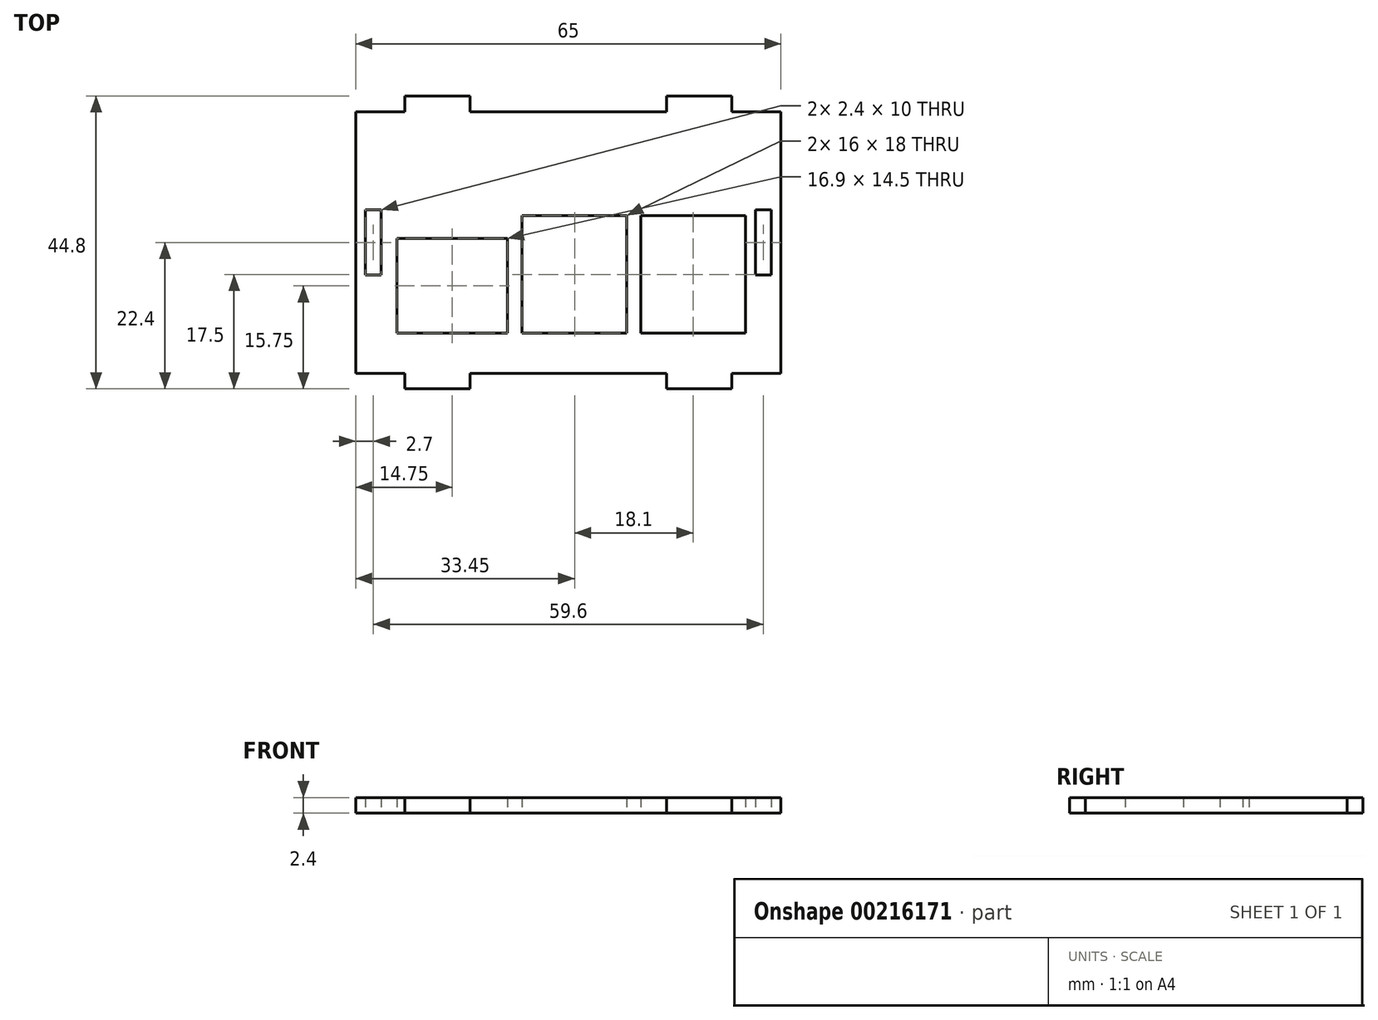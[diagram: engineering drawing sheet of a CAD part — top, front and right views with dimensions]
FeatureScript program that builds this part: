
annotation { "Feature Type Name" : "Feature", "Feature Type Description" : "" }
export const myFeature = defineFeature(function(context is Context, id is Id, definition is map)
    precondition{}
    {
        {
            var Q0;
            Q0=qCreatedBy(makeId("Top.planeOp"),FACE);
            var sketch = newSketch(context, id + "F0", { "sketchPlane" : qUnion([Q0])});
            skLineSegment(sketch, "E0.bottom", {"start": v(32.5, 20) * mm, "end": v(25, 20) * mm});
            skLineSegment(sketch, "E0.top", {"start": v(32.5, -20) * mm, "end": v(25, -20) * mm});
            skLineSegment(sketch, "E0.left", {"start": v(32.5, 20) * mm, "end": v(32.5, -20) * mm});
            skLineSegment(sketch, "E0.right", {"start": v(-32.5, 20) * mm, "end": v(-32.5, -20) * mm});
            skPoint(sketch, "E0.middle", {"position": v(0, 0) * mm});
            skLineSegment(sketch, "E1.bottom", {"start": v(-15, 22.4) * mm, "end": v(-25, 22.4) * mm});
            skLineSegment(sketch, "E1.left", {"start": v(-15, 22.4) * mm, "end": v(-15, 20) * mm});
            skLineSegment(sketch, "E1.right", {"start": v(-25, 22.4) * mm, "end": v(-25, 20) * mm});
            skPoint(sketch, "E1.middle", {"position": v(-20, 20) * mm});
            skLineSegment(sketch, "E2.bottom", {"start": v(25, 22.4) * mm, "end": v(15, 22.4) * mm});
            skLineSegment(sketch, "E2.left", {"start": v(25, 22.4) * mm, "end": v(25, 20) * mm});
            skLineSegment(sketch, "E2.right", {"start": v(15, 22.4) * mm, "end": v(15, 20) * mm});
            skPoint(sketch, "E2.middle", {"position": v(20, 20) * mm});
            skLineSegment(sketch, "E3.top", {"start": v(-15, -22.4) * mm, "end": v(-25, -22.4) * mm});
            skLineSegment(sketch, "E3.left", {"start": v(-15, -20) * mm, "end": v(-15, -22.4) * mm});
            skLineSegment(sketch, "E3.right", {"start": v(-25, -20) * mm, "end": v(-25, -22.4) * mm});
            skPoint(sketch, "E3.middle", {"position": v(-20, -20) * mm});
            skLineSegment(sketch, "E4.top", {"start": v(25, -22.4) * mm, "end": v(15, -22.4) * mm});
            skLineSegment(sketch, "E4.left", {"start": v(25, -20) * mm, "end": v(25, -22.4) * mm});
            skLineSegment(sketch, "E4.right", {"start": v(15, -20) * mm, "end": v(15, -22.4) * mm});
            skPoint(sketch, "E4.middle", {"position": v(20, -20) * mm});
            skPoint(sketch, "E5.middle", {"position": v(0, -20) * mm});
            skLineSegment(sketch, "E6.trimOffspring", {"start": v(-25, 20) * mm, "end": v(-32.5, 20) * mm});
            skLineSegment(sketch, "E7.trimOffspring", {"start": v(15, 20) * mm, "end": v(-15, 20) * mm});
            skLineSegment(sketch, "E8.trimOffspring", {"start": v(15, -20) * mm, "end": v(7.5, -20) * mm});
            skLineSegment(sketch, "E9.trimOffspring", {"start": v(7.5, -20) * mm, "end": v(-15, -20) * mm});
            skLineSegment(sketch, "E10.trimOffspring", {"start": v(-25, -20) * mm, "end": v(-32.5, -20) * mm});
            skLineSegment(sketch, "E11.bottom", {"start": v(-28.6, 5) * mm, "end": v(-31, 5) * mm});
            skLineSegment(sketch, "E11.top", {"start": v(-28.6, -5) * mm, "end": v(-31, -5) * mm});
            skLineSegment(sketch, "E11.left", {"start": v(-28.6, 5) * mm, "end": v(-28.6, -5) * mm});
            skLineSegment(sketch, "E11.right", {"start": v(-31, 5) * mm, "end": v(-31, -5) * mm});
            skPoint(sketch, "E11.middle", {"position": v(-29.8, 0) * mm});
            skLineSegment(sketch, "E12.bottom", {"start": v(31, 5) * mm, "end": v(28.6, 5) * mm});
            skLineSegment(sketch, "E12.top", {"start": v(31, -5) * mm, "end": v(28.6, -5) * mm});
            skLineSegment(sketch, "E12.left", {"start": v(31, 5) * mm, "end": v(31, -5) * mm});
            skLineSegment(sketch, "E12.right", {"start": v(28.6, 5) * mm, "end": v(28.6, -5) * mm});
            skPoint(sketch, "E12.middle", {"position": v(29.8, 0) * mm});
            skLineSegment(sketch, "E13.bottom", {"start": v(-26.2, 0.6) * mm, "end": v(-9.3, 0.6) * mm});
            skLineSegment(sketch, "E13.top", {"start": v(-26.2, -13.9) * mm, "end": v(-9.3, -13.9) * mm});
            skLineSegment(sketch, "E13.left", {"start": v(-26.2, 0.6) * mm, "end": v(-26.2, -13.9) * mm});
            skLineSegment(sketch, "E13.right", {"start": v(-9.3, 0.6) * mm, "end": v(-9.3, -13.9) * mm});
            skLineSegment(sketch, "E14.bottom", {"start": v(-7.05, 4.1) * mm, "end": v(8.95, 4.1) * mm});
            skLineSegment(sketch, "E14.top", {"start": v(-7.05, -13.9) * mm, "end": v(8.95, -13.9) * mm});
            skLineSegment(sketch, "E14.left", {"start": v(-7.05, 4.1) * mm, "end": v(-7.05, -13.9) * mm});
            skLineSegment(sketch, "E14.right", {"start": v(8.95, 4.1) * mm, "end": v(8.95, -13.9) * mm});
            skLineSegment(sketch, "E15.bottom", {"start": v(11.05, 4.1) * mm, "end": v(27.05, 4.1) * mm});
            skLineSegment(sketch, "E15.top", {"start": v(11.05, -13.9) * mm, "end": v(27.05, -13.9) * mm});
            skLineSegment(sketch, "E15.left", {"start": v(11.05, 4.1) * mm, "end": v(11.05, -13.9) * mm});
            skLineSegment(sketch, "E15.right", {"start": v(27.05, 4.1) * mm, "end": v(27.05, -13.9) * mm});
            skSolve(sketch);
        }
        {
            var Q0;
            Q0 = qSketchRegion(id + "F0", true);
            extrude(context, id + "F1", {"entities" : qUnion([Q0]), "depth" : 2.4 * mm});
        }
    });
